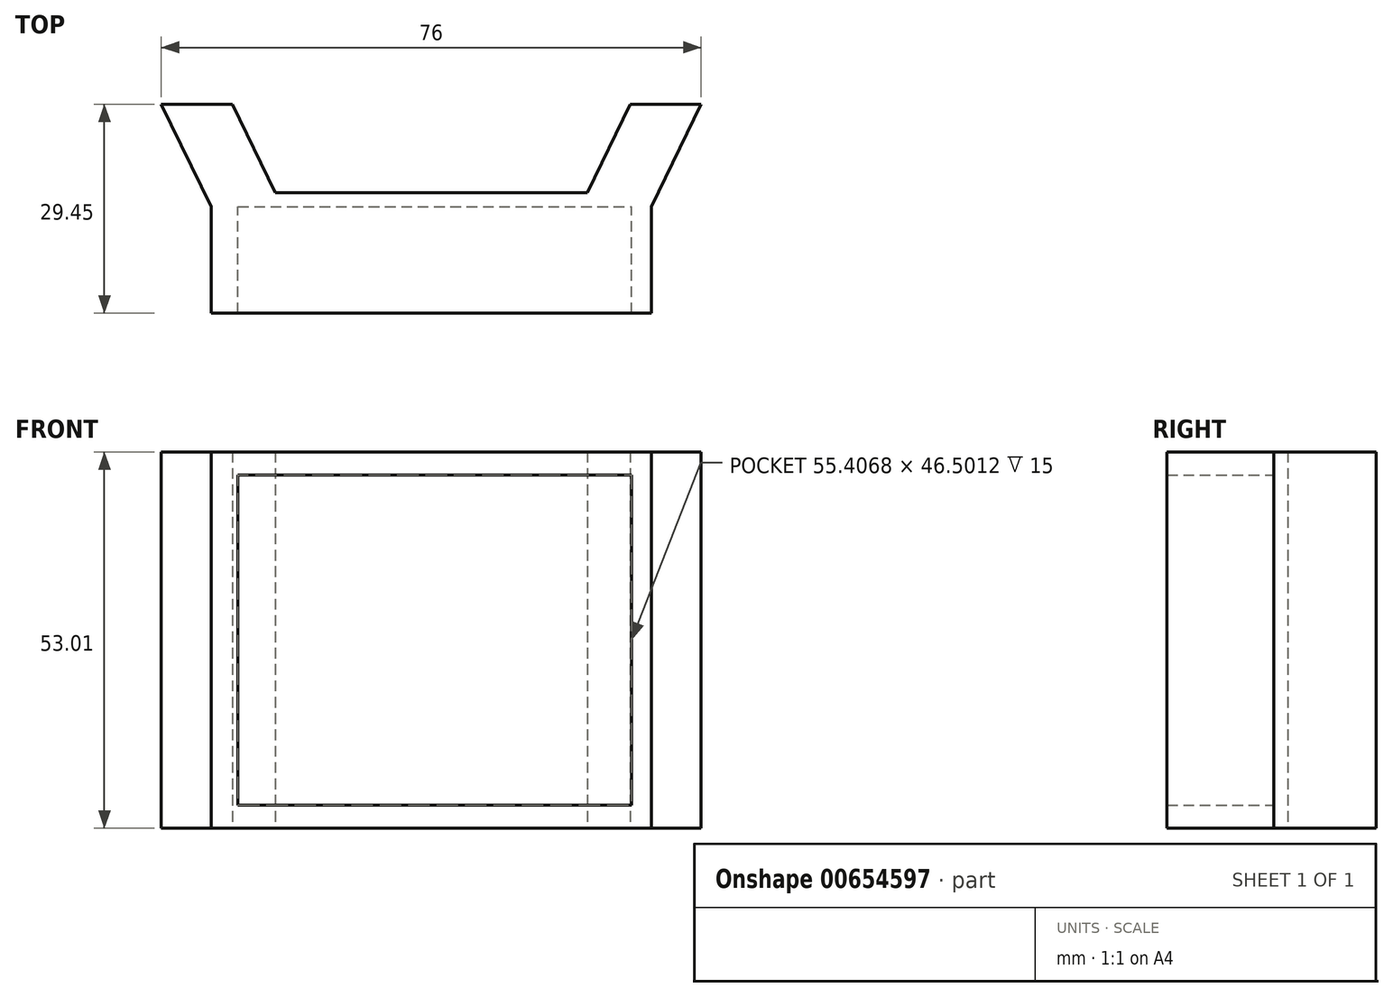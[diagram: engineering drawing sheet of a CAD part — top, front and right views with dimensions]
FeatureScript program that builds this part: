
annotation { "Feature Type Name" : "Feature", "Feature Type Description" : "" }
export const myFeature = defineFeature(function(context is Context, id is Id, definition is map)
    precondition{}
    {
        {
            var Q0;
            Q0=qCreatedBy(makeId("Top.planeOp"),FACE);
            var sketch = newSketch(context, id + "F0", { "sketchPlane" : qUnion([Q0])});
            skLineSegment(sketch, "E0", {"start": v(0, 0) * mm, "end": v(60.52, 0) * mm});
            skLineSegment(sketch, "E1", {"start": v(-8.48, 14.45) * mm, "end": v(1.52, 14.45) * mm, "construction": true});
            skLineSegment(sketch, "E2", {"start": v(60.52, 0) * mm, "end": v(67.52, 14.45) * mm});
            skLineSegment(sketch, "E3", {"start": v(67.52, 14.45) * mm, "end": v(57.52, 14.45) * mm});
            skLineSegment(sketch, "E4", {"start": v(57.52, 14.45) * mm, "end": v(51.49, 2) * mm});
            skLineSegment(sketch, "E5", {"start": v(51.49, 2) * mm, "end": v(7.55, 2) * mm});
            skLineSegment(sketch, "E6", {"start": v(7.55, 2) * mm, "end": v(1.52, 14.45) * mm});
            skLineSegment(sketch, "E7", {"start": v(1.52, 14.45) * mm, "end": v(-8.48, 14.45) * mm});
            skLineSegment(sketch, "E8", {"start": v(-8.48, 14.45) * mm, "end": v(-1.48, 0) * mm});
            skLineSegment(sketch, "E9.trimOffspring", {"start": v(57.52, 14.45) * mm, "end": v(85.23, 14.45) * mm, "construction": true});
            skLineSegment(sketch, "E10.trimOffspring", {"start": v(7.55, 2) * mm, "end": v(51.49, 2) * mm, "construction": true});
            skPoint(sketch, "E11.end.orphan", {"position": v(-8.48, 0) * mm});
            skLineSegment(sketch, "E12", {"start": v(-1.48, 0) * mm, "end": v(0, 0) * mm});
            skSolve(sketch);
        }
        {
            var Q0;
            Q0=makeQuery(id+"F0.imprint","IMPRINT",FACE,{"disambiguationData":[TD([[makeQuery(id+"F0.imprint","IMPRINT",EDGE,{"derivedFrom":sQuery(id+"F0.wireOp",EDGE,"E0")}),1.0]])]});
            extrude(context, id + "F1", {"entities" : qUnion([Q0]), "depth" : 53 * mm, "offsetDistance" : 25 * mm});
        }
        {
            var Q0;
            Q0=makeQuery(id+"F1.opExtrude","SWEPT_FACE",FACE,{"disambiguationData":[OSD([sQuery(id+"F0.wireOp",EDGE,"E0"),sQuery(id+"F0.wireOp",EDGE,"E12")])]});
            var sketch = newSketch(context, id + "F2", { "sketchPlane" : qUnion([Q0])});
            skLineSegment(sketch, "E13.bottom", {"start": v(-1.48, 53) * mm, "end": v(60.52, 53) * mm});
            skLineSegment(sketch, "E13.top", {"start": v(-1.48, 0) * mm, "end": v(60.52, 0) * mm});
            skLineSegment(sketch, "E13.left", {"start": v(-1.48, 53) * mm, "end": v(-1.48, 0) * mm});
            skLineSegment(sketch, "E13.right", {"start": v(60.52, 53) * mm, "end": v(60.52, 0) * mm});
            skLineSegment(sketch, "E14.bottom", {"start": v(2.31, 49.77) * mm, "end": v(57.72, 49.77) * mm});
            skLineSegment(sketch, "E14.top", {"start": v(2.31, 3.27) * mm, "end": v(57.72, 3.27) * mm});
            skLineSegment(sketch, "E14.left", {"start": v(2.31, 49.77) * mm, "end": v(2.31, 3.27) * mm});
            skLineSegment(sketch, "E14.right", {"start": v(57.72, 49.77) * mm, "end": v(57.72, 3.27) * mm});
            skSolve(sketch);
        }
        {
            var Q0;
            Q0=makeQuery(id+"F2.imprint","IMPRINT",FACE,{"disambiguationData":[TD([[makeQuery(id+"F2.imprint","IMPRINT",EDGE,{"derivedFrom":sQuery(id+"F2.wireOp",EDGE,"E13.bottom")}),-1.0]])]});
            extrude(context, id + "F3", {"entities" : qUnion([Q0]), "operationType" : NewBodyOperationType.ADD, "depth" : 15 * mm, "offsetDistance" : 25 * mm});
        }
    });
